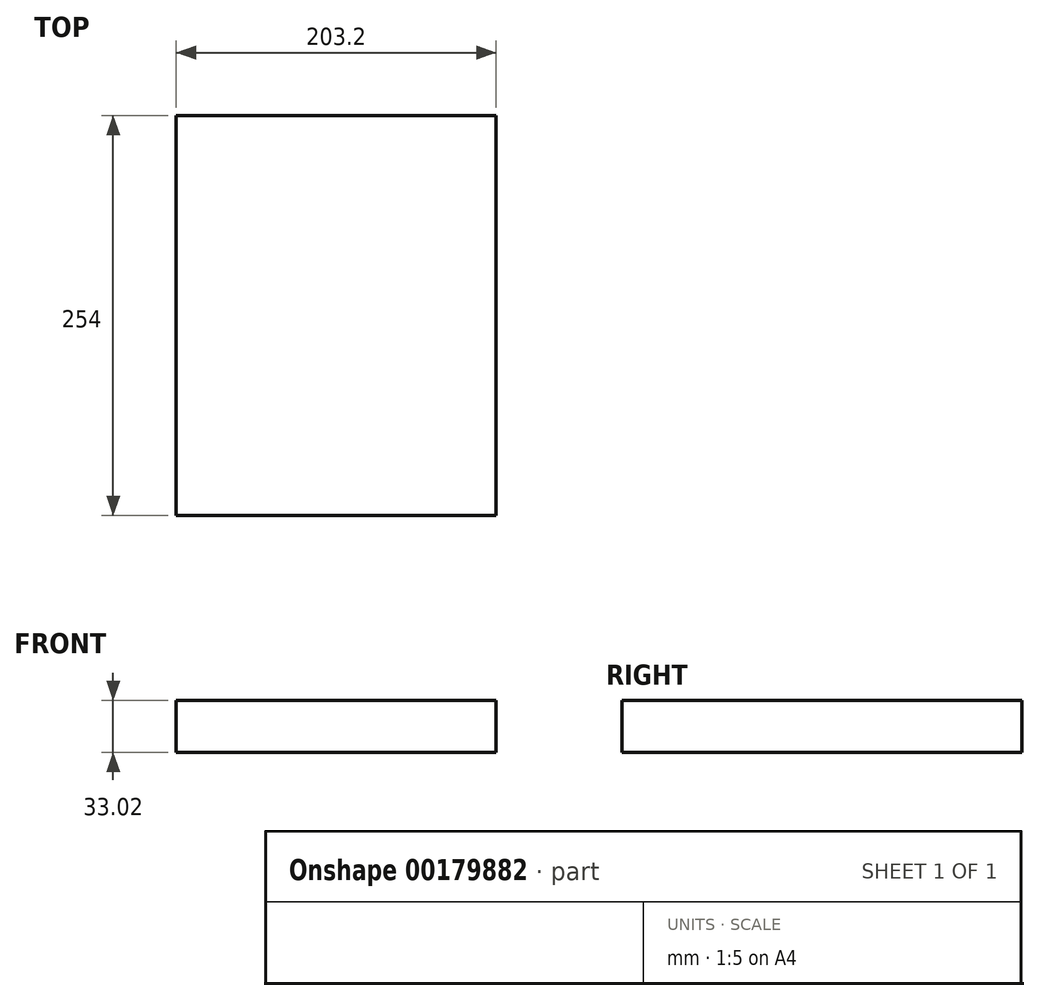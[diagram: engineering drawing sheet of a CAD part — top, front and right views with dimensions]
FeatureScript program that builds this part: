
annotation { "Feature Type Name" : "Feature", "Feature Type Description" : "" }
export const myFeature = defineFeature(function(context is Context, id is Id, definition is map)
    precondition{}
    {
        {
            var Q0;
            Q0=qCreatedBy(makeId("Front.planeOp"),FACE);
            var sketch = newSketch(context, id + "F0", { "sketchPlane" : qUnion([Q0])});
            skLineSegment(sketch, "E0.bottom", {"start": v(-101.6, 16.51) * mm, "end": v(101.6, 16.51) * mm});
            skLineSegment(sketch, "E0.top", {"start": v(-101.6, -16.51) * mm, "end": v(101.6, -16.51) * mm});
            skLineSegment(sketch, "E0.left", {"start": v(-101.6, 16.51) * mm, "end": v(-101.6, -16.5) * mm});
            skLineSegment(sketch, "E0.right", {"start": v(101.6, 16.51) * mm, "end": v(101.6, -16.5) * mm});
            skPoint(sketch, "E0.middle", {"position": v(0, 0) * mm});
            skSolve(sketch);
        }
        {
            var Q0;
            Q0=makeQuery(id+"F0.imprint","IMPRINT",FACE,{"disambiguationData":[TD([[makeQuery(id+"F0.imprint","IMPRINT",EDGE,{"derivedFrom":sQuery(id+"F0.wireOp",EDGE,"E0.bottom")}),-1.0]])]});
            extrude(context, id + "F1", {"entities" : qUnion([Q0]), "depth" : 254 * mm});
        }
    });
